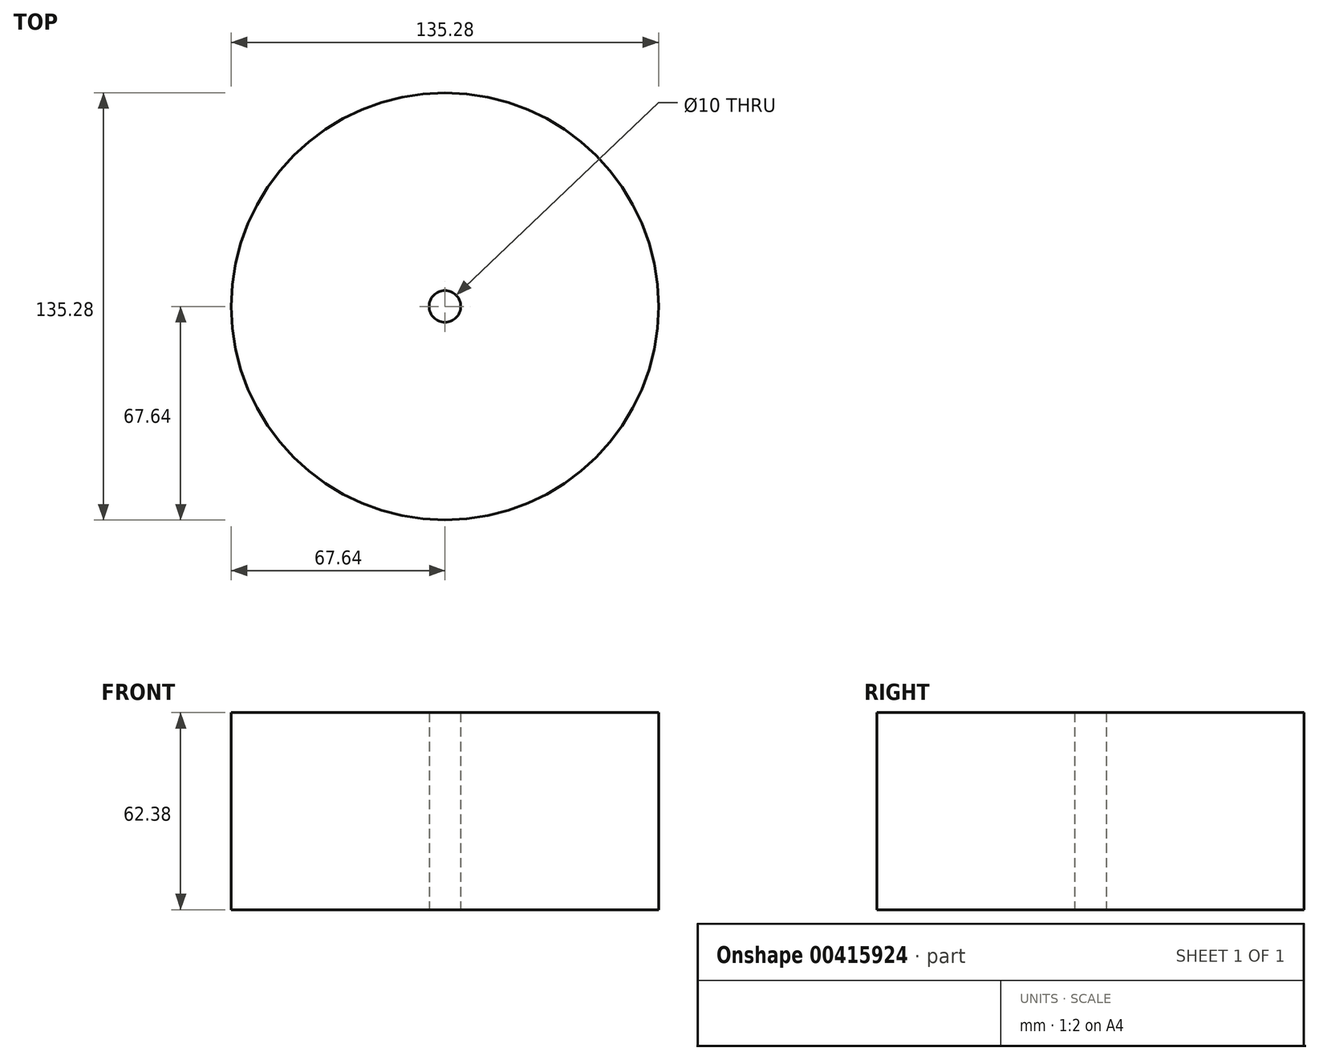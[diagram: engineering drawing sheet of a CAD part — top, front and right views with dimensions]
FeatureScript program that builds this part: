
annotation { "Feature Type Name" : "Feature", "Feature Type Description" : "" }
export const myFeature = defineFeature(function(context is Context, id is Id, definition is map)
    precondition{}
    {
        {
            var Q0;
            Q0=qCreatedBy(makeId("Top.planeOp"),FACE);
            var sketch = newSketch(context, id + "F0", { "sketchPlane" : qUnion([Q0])});
            skCircle(sketch, "E0", {"center": v(0, 0) * mm, "radius": 67.64 * mm});
            skSolve(sketch);
        }
        {
            var Q0;
            Q0=makeQuery(id+"F0.imprint","IMPRINT",FACE,{"disambiguationData":[TD([[makeQuery(id+"F0.imprint","IMPRINT",EDGE,{"derivedFrom":sQuery(id+"F0.wireOp",EDGE,"E0")}),1.0]])]});
            extrude(context, id + "F1", {"entities" : qUnion([Q0]), "depth" : 62.38 * mm});
        }
        {
            var Q0;
            Q0=qCreatedBy(makeId("Top.planeOp"),FACE);
            var sketch = newSketch(context, id + "F2", { "sketchPlane" : qUnion([Q0])});
            skPoint(sketch, "E1", {"position": v(0, 0) * mm});
            skSolve(sketch);
        }
        {
            var Q0;
            Q0=sQuery(id+"F2.wireOp",VERTEX,"E1");
            var Q1;
            Q1=makeQuery(id+"F1.opExtrude","SWEPT_BODY",BODY,{"disambiguationData":[OSD([sQuery(id+"F0.wireOp",EDGE,"E0")])]});
            hole(context, id + "F3", {"style" : HoleStyle.SIMPLE, "endStyle" : HoleEndStyle.THROUGH, "oppositeDirection" : true, "holeDiameter" : 10 * mm, "isTappedThrough" : true, "tappedDepth" : 12 * mm, "tapClearance" : 3, "locations" : qUnion([Q0]), "scope" : qUnion([Q1])});
        }
    });
